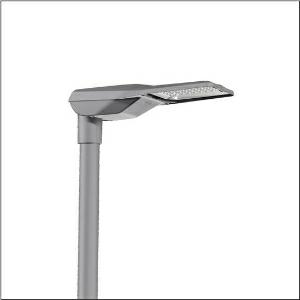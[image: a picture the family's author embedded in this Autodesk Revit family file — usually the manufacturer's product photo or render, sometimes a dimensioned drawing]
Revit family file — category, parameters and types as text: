
# Revit family: streetlight_sl_21_iq_mini___st1_0ab_5xe2m31d08jb_643a
name_source: partatom
category: Lighting Fixtures
units: mm (PartAtom-declared; Revit-internal decimal feet)

## family parameters
Cut with Voids When Loaded = No
Host = Face
Light Source = No
Part Type = Normal
Room Calculation Point = No
Round Connector Dimension = Use Diameter
Shared = No

## types (1)
- --- (1 x LED, 9530 lm, 71.6 W, 3000K)
    Apparent Load = 72 VA
    CIE Flux Codes = 40 74 97 100 100
    Color Rendering = 70
    Color Temperature = 3000K
    Default Elevation = 1800 mm
    Description = Streetlight SL 21 iQ mini, mast luminaire, primary light control with lens, of PMMA, primary optical cover: cover, of toughened safety glass, transparent, light distribution: ST1.0aB, light emission: direct distribution, primary light characteristic: asymmetric, installation type: post-top, side-entry, LED, High Power LED, rated luminous flux: 9.530lm, luminous efficacy: 133lm/W, light colour: 730, colour temperature: 3000K, control gear: iQ-Comfort, control: Auto-Match, Temp-Guard, Lumen-Switch, Night-Set, Smart-Wire, Light-Fading, Desk-Remote (wireless, voltage-free reading and setting of iQ features in the workshop via application-optimized NFC function/RFID function), optimised constant luminous flux control (CLO 2.0), pre-setting: linear dimming characteristic, mains connection: 220..240V, AC, 50/60Hz, start of lifetime: 72W, end of service life: 75W, reduction: 33W, luminaire housing, of diecast aluminium, powder-coated, SITECO metallic grey (DB 702S), corrosivity category C5 high according to DIN EN ISO 12944, please order mast flange separately, inclination adjustable: 0°, 5°, 10°, 15°, sealing non-destructively replaceable, multi-level sealing system, length: 628mm, width: 235mm, height: 110mm, mast flange for spigot size: 42mm (side-entry): 5XC10008XM4, 60/48mm (side-entry/post-top): 5XC10108XM2, 76/60mm (side-entry/post-top): 5XC10108XM1, mounting height: 4..8m, protection rating (complete): IP66, insulation class (complete): insulation class II (safety insulation), certification: CE, ENEC, ENEC+, VDE, impact resistance: IK10, permissible operating ambient temperature for outdoor applications: -40..+50°C, standard-compliant lighting for roads and squares, packaging unit: 1 piece

Light Distribution: ST1.0aB
    Height = 110 mm
    Lamp = 1 x LED
    Lamp Light Flux = 9530 lm
    Lamp Power = 71.6 W
    Lamp count = 1
    Length = 625 mm
    Luminous efficacy = 133 lm/W
    Manufacturer = Siteco
    ModVariant = No
    Model = 5XE2M31D08JB
    Number of Poles = 1
    OnlyDefault = Yes
    Power Factor = 1
    Product Name = Streetlight SL 21 iQ mini | ST1.0aB
    Product group = mast luminaire | pylon top
    ProductGroupID = 6100
    Protection Class = Protection class II
    Protection Degree = IP 66
    RLX_Detail_Level = 1
    RLX_Emergency_Light_Flux = 0 lm
    RLX_Emergency_Type = 0
    RLX_Emergency_Type_DB = No
    RlxData = <blob elided: 26313 chars, md5=3ec338e6>
    Socket = socket
    Standby Power = 0 W
    System Light Flux = 9530 lm
    System Power = 72 W
    Type Comments = factory setting: luminous flux: 100 % | dim-lin: 254 | 746 mA
    Type Image = l_1003519.jpg
    URL = http://relux.com
    VarID = @adj_167855
    Voltage = 0 V
    Weight = 0.00 kg
    Width = 234 mm

## geometry (parser evidence)
native form markers: Blend x4, Sweep x10
no freeform markers — native parametric forms only
